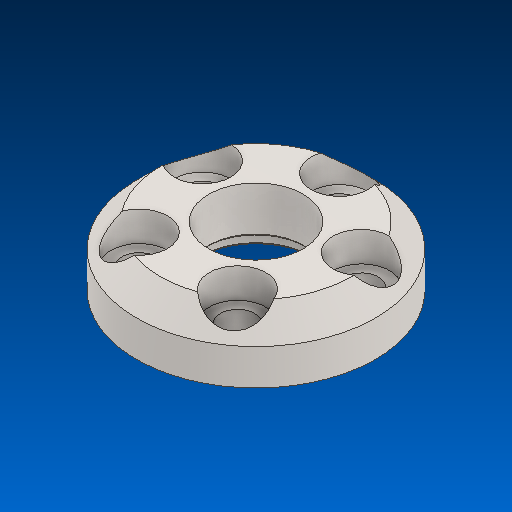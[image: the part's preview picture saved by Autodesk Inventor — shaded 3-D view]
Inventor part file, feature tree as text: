
AUTODESK INVENTOR PART (.ipt)
format: ipt  version: 2022.2 (Build 262287000, 287)  size: 173,568 bytes
history: native  units: in
note: dims shown in document units (in); Inventor stores cm internally (conversion verified against a paired STEP export)
features: chamfer x1
ambient origin geometry x8: Origin, YZ Plane, XZ Plane, XY Plane, X Axis, Y Axis, Z Axis, Center Point
bodies: Solid1 (feature_tree)
feature tree (1):
  chamfer  "Chamfer2"  [1 undecoded]
note: 1 required parameter value undecoded (feature->parameter linkage not recoverable at this tier; creation-order binding heuristic only, values carry confidence <= 0.55)
